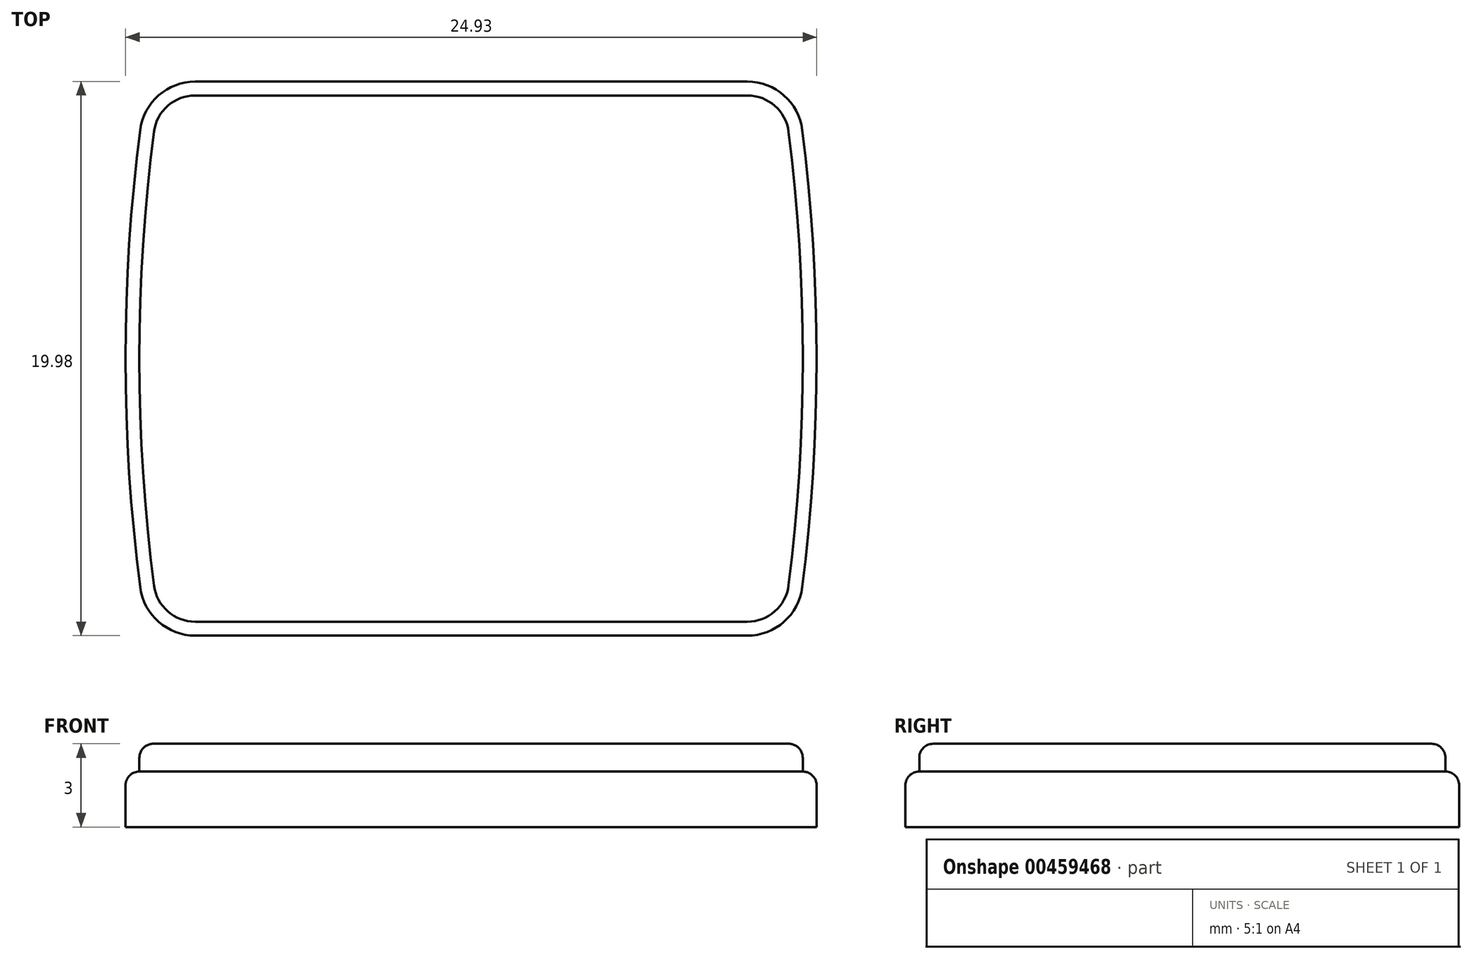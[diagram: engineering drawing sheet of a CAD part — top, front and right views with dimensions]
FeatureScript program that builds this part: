
annotation { "Feature Type Name" : "Feature", "Feature Type Description" : "" }
export const myFeature = defineFeature(function(context is Context, id is Id, definition is map)
    precondition{}
    {
        {
            var Q0;
            Q0=qCreatedBy(makeId("Top.planeOp"),FACE);
            var sketch = newSketch(context, id + "F0", { "sketchPlane" : qUnion([Q0])});
            skPoint(sketch, "E0.endSnap0", {"position": v(23.7, 10) * mm});
            skPoint(sketch, "E1.visualSharp", {"position": v(23.7, 20) * mm});
            skArc(sketch, "E1.filletArc", {"start": v(23.7, 18.24) * mm, "mid": v(23.03, 19.49) * mm, "end": v(21.7, 19.99) * mm});
            skPoint(sketch, "E2.visualSharp", {"position": v(23.7, 0) * mm});
            skArc(sketch, "E2.filletArc", {"start": v(21.7, 0.01) * mm, "mid": v(23.03, 0.51) * mm, "end": v(23.7, 1.76) * mm});
            skPoint(sketch, "E3.visualSharp", {"position": v(0, 0) * mm});
            skArc(sketch, "E3.filletArc", {"start": v(-0.2, 1.75) * mm, "mid": v(0.47, 0.5) * mm, "end": v(1.8, 0.01) * mm});
            skPoint(sketch, "E4.visualSharp", {"position": v(0, 20) * mm});
            skArc(sketch, "E4.filletArc", {"start": v(1.8, 19.99) * mm, "mid": v(0.47, 19.5) * mm, "end": v(-0.2, 18.25) * mm});
            skLineSegment(sketch, "E5", {"start": v(23.7, 10) * mm, "end": v(24.2, 10) * mm, "construction": true});
            skLineSegment(sketch, "E6", {"start": v(-0.22, 10) * mm, "end": v(-0.72, 10) * mm, "construction": true});
            skLineSegment(sketch, "E7", {"start": v(11.75, -0.01) * mm, "end": v(11.75, -0.51) * mm, "construction": true});
            skLineSegment(sketch, "E8", {"start": v(11.75, 20.01) * mm, "end": v(11.75, 20.51) * mm, "construction": true});
            skArc(sketch, "E9", {"start": v(23.7, 1.76) * mm, "mid": v(24.2, 10) * mm, "end": v(23.7, 18.24) * mm});
            skArc(sketch, "E10", {"start": v(21.7, 19.99) * mm, "mid": v(11.75, 20.51) * mm, "end": v(1.8, 19.99) * mm, "construction": true});
            skArc(sketch, "E11", {"start": v(-0.2, 18.25) * mm, "mid": v(-0.72, 10) * mm, "end": v(-0.2, 1.75) * mm});
            skArc(sketch, "E12", {"start": v(1.8, 0.01) * mm, "mid": v(11.75, -0.51) * mm, "end": v(21.7, 0.01) * mm, "construction": true});
            skLineSegment(sketch, "E13", {"start": v(1.8, 0.01) * mm, "end": v(21.7, 0.01) * mm});
            skLineSegment(sketch, "E14", {"start": v(1.8, 19.99) * mm, "end": v(21.7, 19.99) * mm});
            skSolve(sketch);
        }
        {
            var Q0;
            Q0=makeQuery(id+"F0.imprint","IMPRINT",FACE,{"disambiguationData":[TD([[makeQuery(id+"F0.imprint","IMPRINT",EDGE,{"derivedFrom":sQuery(id+"F0.wireOp",EDGE,"E1.filletArc")}),1.0]])]});
            extrude(context, id + "F1", {"entities" : qUnion([Q0]), "depth" : 2 * mm});
        }
        {
            var Q0;
            Q0=makeQuery(id+"F1.opExtrude","CAP_FACE",FACE,{"disambiguationData":[OSD([sQuery(id+"F0.wireOp",EDGE,"E1.filletArc"),sQuery(id+"F0.wireOp",EDGE,"E2.filletArc"),sQuery(id+"F0.wireOp",EDGE,"E3.filletArc"),sQuery(id+"F0.wireOp",EDGE,"E4.filletArc"),sQuery(id+"F0.wireOp",EDGE,"E9"),sQuery(id+"F0.wireOp",EDGE,"E10"),sQuery(id+"F0.wireOp",EDGE,"E11"),sQuery(id+"F0.wireOp",EDGE,"E12")])],"isStart":false});
            var sketch = newSketch(context, id + "F2", { "sketchPlane" : qUnion([Q0])});
            skLineSegment(sketch, "E15.0", {"start": v(1.8, 19.49) * mm, "end": v(21.7, 19.49) * mm});
            skArc(sketch, "E15.1", {"start": v(23.2, 18.18) * mm, "mid": v(22.7, 19.11) * mm, "end": v(21.7, 19.49) * mm});
            skArc(sketch, "E15.2", {"start": v(1.8, 19.49) * mm, "mid": v(0.8, 19.12) * mm, "end": v(0.3, 18.18) * mm});
            skArc(sketch, "E15.3", {"start": v(23.2, 1.82) * mm, "mid": v(23.7, 10) * mm, "end": v(23.2, 18.18) * mm});
            skArc(sketch, "E15.4", {"start": v(0.3, 18.18) * mm, "mid": v(-0.22, 10) * mm, "end": v(0.3, 1.82) * mm});
            skArc(sketch, "E15.5", {"start": v(0.3, 1.82) * mm, "mid": v(0.8, 0.88) * mm, "end": v(1.8, 0.51) * mm});
            skLineSegment(sketch, "E15.6", {"start": v(1.8, 0.51) * mm, "end": v(21.7, 0.51) * mm});
            skArc(sketch, "E15.7", {"start": v(21.7, 0.51) * mm, "mid": v(22.7, 0.89) * mm, "end": v(23.2, 1.82) * mm});
            skSolve(sketch);
        }
        {
            var Q0;
            Q0 = qSketchRegion(id + "F2", true);
            extrude(context, id + "F3", {"entities" : qUnion([Q0]), "operationType" : NewBodyOperationType.ADD, "depth" : 1 * mm});
        }
        {
            var Q0;
            Q0=makeQuery(id+"F3.opExtrude","CAP_EDGE",EDGE,{"disambiguationData":[OSD([sQuery(id+"F2.wireOp",EDGE,"77a875c0-5ee6-4c69-aeb2-6cd3550bd4b3.6")])],"isStart":false});
            var Q1;
            Q1=makeQuery(id+"F1.opExtrude","CAP_EDGE",EDGE,{"disambiguationData":[OSD([sQuery(id+"F0.wireOp",EDGE,"E12")])],"isStart":false});
            var Q2;
            Q2=makeQuery(id+"F1.opExtrude","CAP_EDGE",EDGE,{"disambiguationData":[OSD([sQuery(id+"F0.wireOp",EDGE,"E10")])],"isStart":false});
            var Q3;
            Q3=makeQuery(id+"F1.opExtrude","CAP_EDGE",EDGE,{"disambiguationData":[OSD([sQuery(id+"F0.wireOp",EDGE,"E2.filletArc")])],"isStart":false});
            var Q4;
            Q4=makeQuery(id+"F3.opExtrude","CAP_EDGE",EDGE,{"disambiguationData":[OSD([sQuery(id+"F2.wireOp",EDGE,"77a875c0-5ee6-4c69-aeb2-6cd3550bd4b3.7")])],"isStart":false});
            var Q5;
            Q5=makeQuery(id+"F1.opExtrude","CAP_EDGE",EDGE,{"disambiguationData":[OSD([sQuery(id+"F0.wireOp",EDGE,"E3.filletArc")])],"isStart":false});
            var Q6;
            Q6=makeQuery(id+"F3.opExtrude","CAP_EDGE",EDGE,{"disambiguationData":[OSD([sQuery(id+"F2.wireOp",EDGE,"77a875c0-5ee6-4c69-aeb2-6cd3550bd4b3.3")])],"isStart":false});
            var Q7;
            Q7=makeQuery(id+"F1.opExtrude","CAP_EDGE",EDGE,{"disambiguationData":[OSD([sQuery(id+"F0.wireOp",EDGE,"E9")])],"isStart":false});
            var Q8;
            Q8=makeQuery(id+"F1.opExtrude","CAP_EDGE",EDGE,{"disambiguationData":[OSD([sQuery(id+"F0.wireOp",EDGE,"E11")])],"isStart":false});
            var Q9;
            Q9=makeQuery(id+"F1.opExtrude","CAP_EDGE",EDGE,{"disambiguationData":[OSD([sQuery(id+"F0.wireOp",EDGE,"E4.filletArc")])],"isStart":false});
            var Q10;
            Q10=makeQuery(id+"F3.opExtrude","CAP_EDGE",EDGE,{"disambiguationData":[OSD([sQuery(id+"F2.wireOp",EDGE,"77a875c0-5ee6-4c69-aeb2-6cd3550bd4b3.5")])],"isStart":false});
            var Q11;
            Q11=makeQuery(id+"F3.opExtrude","CAP_EDGE",EDGE,{"disambiguationData":[OSD([sQuery(id+"F2.wireOp",EDGE,"77a875c0-5ee6-4c69-aeb2-6cd3550bd4b3.2")])],"isStart":false});
            var Q12;
            Q12=makeQuery(id+"F1.opExtrude","CAP_EDGE",EDGE,{"disambiguationData":[OSD([sQuery(id+"F0.wireOp",EDGE,"E1.filletArc")])],"isStart":false});
            var Q13;
            Q13=makeQuery(id+"F3.opExtrude","CAP_EDGE",EDGE,{"disambiguationData":[OSD([sQuery(id+"F2.wireOp",EDGE,"77a875c0-5ee6-4c69-aeb2-6cd3550bd4b3.4")])],"isStart":false});
            var Q14;
            Q14=makeQuery(id+"F3.opExtrude","CAP_EDGE",EDGE,{"disambiguationData":[OSD([sQuery(id+"F2.wireOp",EDGE,"77a875c0-5ee6-4c69-aeb2-6cd3550bd4b3.0")])],"isStart":false});
            var Q15;
            Q15=makeQuery(id+"F3.opExtrude","CAP_EDGE",EDGE,{"disambiguationData":[OSD([sQuery(id+"F2.wireOp",EDGE,"77a875c0-5ee6-4c69-aeb2-6cd3550bd4b3.1")])],"isStart":false});
            var Q16;
            Q16=makeQuery(id+"F3.opExtrude","CAP_EDGE",EDGE,{"disambiguationData":[OSD([sQuery(id+"F2.wireOp",EDGE,"E15.6")])],"isStart":false});
            var Q17;
            Q17=makeQuery(id+"F3.opExtrude","CAP_EDGE",EDGE,{"disambiguationData":[OSD([sQuery(id+"F2.wireOp",EDGE,"E15.5")])],"isStart":false});
            var Q18;
            Q18=makeQuery(id+"F3.opExtrude","CAP_EDGE",EDGE,{"disambiguationData":[OSD([sQuery(id+"F2.wireOp",EDGE,"E15.4")])],"isStart":false});
            var Q19;
            Q19=makeQuery(id+"F3.opExtrude","CAP_EDGE",EDGE,{"disambiguationData":[OSD([sQuery(id+"F2.wireOp",EDGE,"E15.0")])],"isStart":false});
            var Q20;
            Q20=makeQuery(id+"F3.opExtrude","CAP_EDGE",EDGE,{"disambiguationData":[OSD([sQuery(id+"F2.wireOp",EDGE,"E15.1")])],"isStart":false});
            var Q21;
            Q21=makeQuery(id+"F3.opExtrude","CAP_EDGE",EDGE,{"disambiguationData":[OSD([sQuery(id+"F2.wireOp",EDGE,"E15.3")])],"isStart":false});
            var Q22;
            Q22=makeQuery(id+"F3.opExtrude","CAP_EDGE",EDGE,{"disambiguationData":[OSD([sQuery(id+"F2.wireOp",EDGE,"E15.2")])],"isStart":false});
            var Q23;
            Q23=makeQuery(id+"F3.opExtrude","CAP_EDGE",EDGE,{"disambiguationData":[OSD([sQuery(id+"F2.wireOp",EDGE,"E15.7")])],"isStart":false});
            fillet(context, id + "F4", {"entities" : qUnion([Q0, Q1, Q2, Q3, Q4, Q5, Q6, Q7, Q8, Q9, Q10, Q11, Q12, Q13, Q14, Q15, Q16, Q17, Q18, Q19, Q20, Q21, Q22, Q23]), "radius" : 0.5 * mm, "tangentPropagation" : true, "allowEdgeOverflow" : false});
        }
    });
